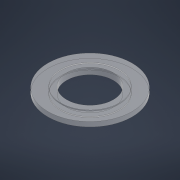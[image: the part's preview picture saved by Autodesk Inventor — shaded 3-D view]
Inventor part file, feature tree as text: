
AUTODESK INVENTOR PART (.ipt)
format: ipt  version: 2021 (Build 250183000, 183)  size: 123,392 bytes
history: native  units: mm
features: other x2, extrude x2, sketch x2
ambient origin geometry x8: Origin, YZ Plane, XZ Plane, XY Plane, X Axis, Y Axis, Z Axis, Center Point
bodies: Body1 (feature_tree)
feature tree (6):
  other  "Apoio Contato"
  other  "Sólido1"
  extrude  "Extrusão1"  Depth=1.0mm
  extrude  "Extrusão2"  Depth=0.12mm
  sketch  "Esboço1"  dims[d0=1.8mm d1=1.0mm]
  sketch  "Esboço2"  dims[d2=0.1mm d3=0.0mm d4=1.25mm d5=0.02mm d6=0.12mm d7=0.0mm d8=0.0mm]
